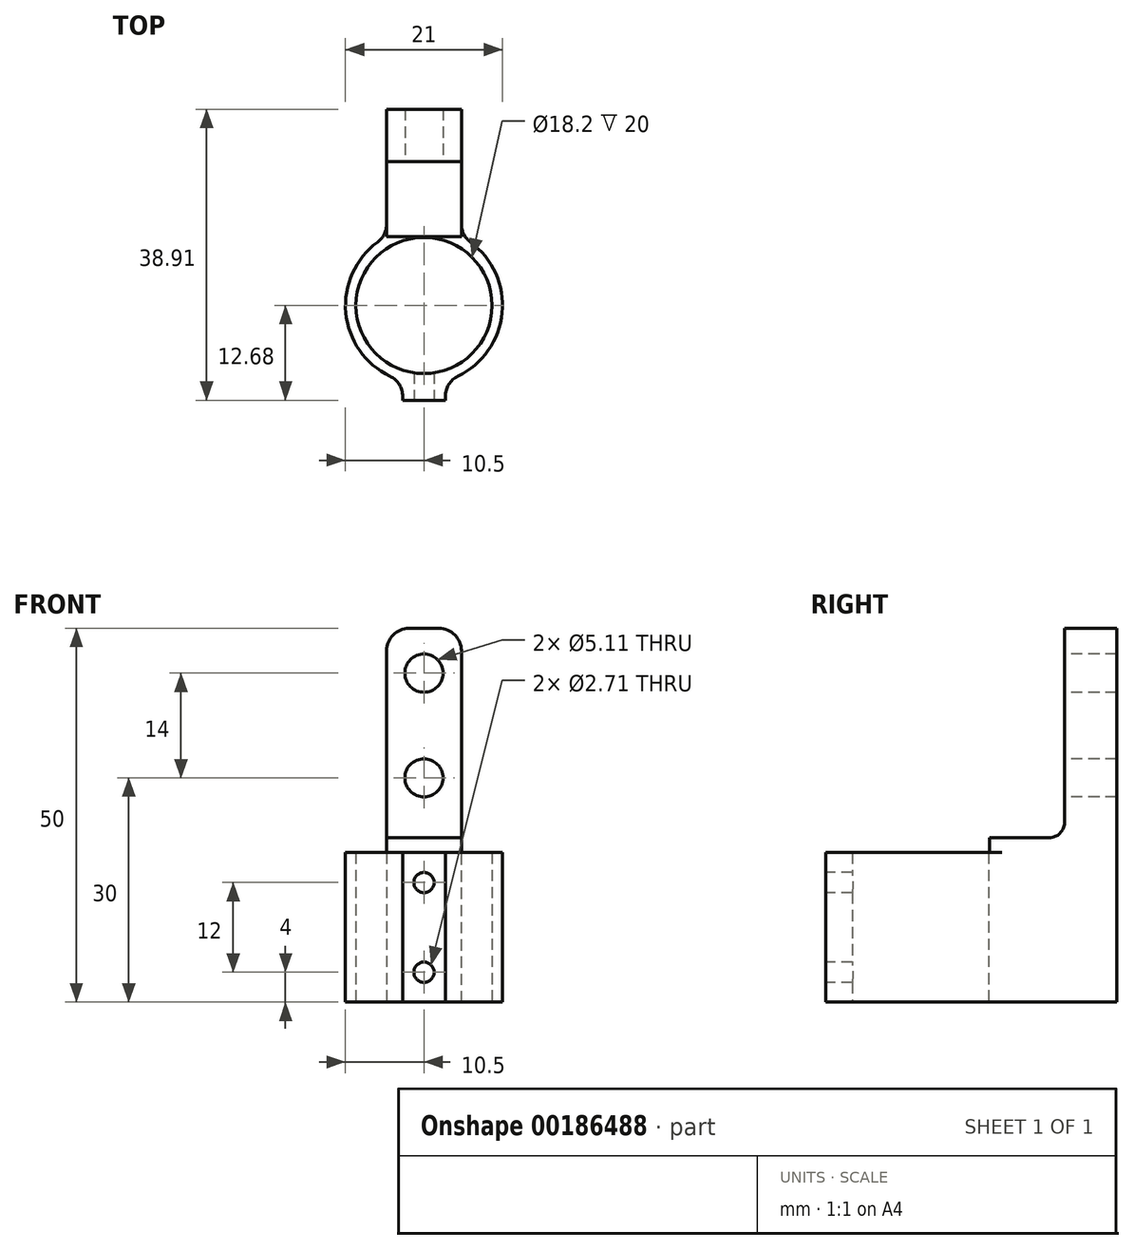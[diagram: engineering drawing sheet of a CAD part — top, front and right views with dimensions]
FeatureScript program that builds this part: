
annotation { "Feature Type Name" : "Feature", "Feature Type Description" : "" }
export const myFeature = defineFeature(function(context is Context, id is Id, definition is map)
    precondition{}
    {
        {
            var Q0;
            Q0=qCreatedBy(makeId("Top.planeOp"),FACE);
            var sketch = newSketch(context, id + "F0", { "sketchPlane" : qUnion([Q0])});
            skCircle(sketch, "E0", {"center": v(0, 0) * mm, "radius": 9.1 * mm});
            skCircle(sketch, "E1", {"center": v(0, 0) * mm, "radius": 10.5 * mm});
            skLineSegment(sketch, "E2.bottom", {"start": v(5, 9.23) * mm, "end": v(-5, 9.23) * mm});
            skLineSegment(sketch, "E2.top", {"start": v(5, 26.23) * mm, "end": v(-5, 26.23) * mm});
            skLineSegment(sketch, "E2.left", {"start": v(5, 9.23) * mm, "end": v(5, 26.23) * mm});
            skLineSegment(sketch, "E2.right", {"start": v(-5, 9.23) * mm, "end": v(-5, 26.23) * mm});
            skLineSegment(sketch, "E3.bottom", {"start": v(-2.85, -10.1) * mm, "end": v(2.85, -10.1) * mm});
            skLineSegment(sketch, "E3.top", {"start": v(-2.85, -12.68) * mm, "end": v(2.85, -12.68) * mm});
            skLineSegment(sketch, "E3.left", {"start": v(-2.85, -10.1) * mm, "end": v(-2.85, -12.68) * mm});
            skLineSegment(sketch, "E3.right", {"start": v(2.85, -10.1) * mm, "end": v(2.85, -12.68) * mm});
            skSolve(sketch);
        }
        {
            var Q0;
            Q0=qSketchRegion(id+"F0",true);
            extrude(context, id + "F1", {"entities" : qUnion([Q0]), "depth" : 20 * mm});
        }
        {
            var Q0;
            Q0=makeQuery(id+"F1.opExtrude","CAP_FACE",FACE,{"disambiguationData":[OSD([sQuery(id+"F0.wireOp",EDGE,"E0"),sQuery(id+"F0.wireOp",EDGE,"E1"),sQuery(id+"F0.wireOp",EDGE,"E2.top"),sQuery(id+"F0.wireOp",EDGE,"E2.left"),sQuery(id+"F0.wireOp",EDGE,"Skpy10Sz-M8vA-u5j2-6a00-2GGWUu09V0g2.top"),sQuery(id+"F0.wireOp",EDGE,"Skpy10Sz-M8vA-u5j2-6a00-2GGWUu09V0g2.left"),sQuery(id+"F0.wireOp",EDGE,"Skpy10Sz-M8vA-u5j2-6a00-2GGWUu09V0g2.right")])],"isStart":false});
            var sketch = newSketch(context, id + "F2", { "sketchPlane" : qUnion([Q0])});
            skLineSegment(sketch, "E4.bottom", {"start": v(5, 26.23) * mm, "end": v(-5, 26.23) * mm});
            skLineSegment(sketch, "E4.top", {"start": v(5, 9.23) * mm, "end": v(-5, 9.23) * mm});
            skLineSegment(sketch, "E4.left", {"start": v(5, 26.23) * mm, "end": v(5, 9.23) * mm});
            skLineSegment(sketch, "E4.right", {"start": v(-5, 26.23) * mm, "end": v(-5, 9.23) * mm});
            skSolve(sketch);
        }
        {
            var Q0;
            Q0=qSketchRegion(id+"F2",true);
            extrude(context, id + "F3", {"entities" : qUnion([Q0]), "operationType" : NewBodyOperationType.ADD, "depth" : 30 * mm});
        }
        {
            var Q0;
            Q0=makeQuery(id+"F3.boolean.opBoolean","MERGE",FACE,{"derivedFrom":[makeQuery(id+"F1.opExtrude","SWEPT_FACE",FACE,{"disambiguationData":[OSD([sQuery(id+"F0.wireOp",EDGE,"E2.left")])]}),makeQuery(id+"F3.opExtrude","SWEPT_FACE",FACE,{"disambiguationData":[OSD([sQuery(id+"F2.wireOp",EDGE,"E4.left")])]})]});
            var sketch = newSketch(context, id + "F4", { "sketchPlane" : qUnion([Q0])});
            skLineSegment(sketch, "E5.bottom", {"start": v(9.23, 50) * mm, "end": v(19.23, 50) * mm});
            skLineSegment(sketch, "E5.top", {"start": v(9.23, 22) * mm, "end": v(19.23, 22) * mm});
            skLineSegment(sketch, "E5.left", {"start": v(9.23, 50) * mm, "end": v(9.23, 22) * mm});
            skLineSegment(sketch, "E5.right", {"start": v(19.23, 50) * mm, "end": v(19.23, 22) * mm});
            skSolve(sketch);
        }
        {
            var Q0;
            Q0 = qSketchRegion(id + "F4", true);
            extrude(context, id + "F5", {"entities" : qUnion([Q0]), "operationType" : NewBodyOperationType.REMOVE, "oppositeDirection" : true, "depth" : 25.4 * mm});
        }
        {
            var Q0;
            Q0=makeQuery(id+"F1.opExtrude","SWEPT_EDGE",EDGE,{"disambiguationData":[OSD([sQuery(id+"F0.wireOp",EDGE,"E1"),sQuery(id+"F0.wireOp",EDGE,"E2.bottom"),sQuery(id+"F0.wireOp",EDGE,"E2.left")])]});
            var Q1;
            Q1=makeQuery(id+"F1.opExtrude","SWEPT_EDGE",EDGE,{"disambiguationData":[OSD([sQuery(id+"F0.wireOp",EDGE,"E1"),sQuery(id+"F0.wireOp",EDGE,"E2.bottom"),sQuery(id+"F0.wireOp",EDGE,"E2.right")])]});
            var Q2;
            Q2=makeQuery(id+"F3.opExtrude","CAP_EDGE",EDGE,{"disambiguationData":[OSD([sQuery(id+"F2.wireOp",EDGE,"E4.right")])],"isStart":false});
            var Q3;
            Q3=makeQuery(id+"F3.opExtrude","CAP_EDGE",EDGE,{"disambiguationData":[OSD([sQuery(id+"F2.wireOp",EDGE,"E4.left")])],"isStart":false});
            var Q4;
            Q4=makeQuery(id+"F1.opExtrude","SWEPT_EDGE",EDGE,{"disambiguationData":[OSD([sQuery(id+"F0.wireOp",EDGE,"E1"),sQuery(id+"F0.wireOp",EDGE,"E3.bottom"),sQuery(id+"F0.wireOp",EDGE,"E3.right")])]});
            var Q5;
            Q5=makeQuery(id+"F1.opExtrude","SWEPT_EDGE",EDGE,{"disambiguationData":[OSD([sQuery(id+"F0.wireOp",EDGE,"E1"),sQuery(id+"F0.wireOp",EDGE,"E3.bottom"),sQuery(id+"F0.wireOp",EDGE,"E3.left")])]});
            fillet(context, id + "F6", {"entities" : qUnion([Q0, Q1, Q2, Q3, Q4, Q5]), "radius" : 3 * mm, "tangentPropagation" : true, "allowEdgeOverflow" : false});
        }
        {
            var Q0;
            Q0=makeQuery(id+"F5.boolean.opBoolean","COPY",EDGE,{"derivedFrom":makeQuery(id+"F5.opExtrude","SWEPT_EDGE",EDGE,{"disambiguationData":[OSD([sQuery(id+"F0.wireOp",EDGE,"E1"),sQuery(id+"F2.wireOp",EDGE,"E4.top"),sQuery(id+"F2.wireOp",EDGE,"E4.left"),sQuery(id+"F4.wireOp",EDGE,"E5.top"),sQuery(id+"F4.wireOp",EDGE,"E5.left")])]})});
            var Q1;
            Q1=makeQuery(id+"F5.boolean.opBoolean","COPY",EDGE,{"derivedFrom":makeQuery(id+"F5.opExtrude","SWEPT_EDGE",EDGE,{"disambiguationData":[OSD([sQuery(id+"F4.wireOp",EDGE,"E5.top"),sQuery(id+"F4.wireOp",EDGE,"E5.right")])]})});
            fillet(context, id + "F7", {"entities" : qUnion([Q0, Q1]), "radius" : 2 * mm, "tangentPropagation" : true, "allowEdgeOverflow" : false});
        }
        {
            var Q0;
            Q0=makeQuery(id+"F5.boolean.opBoolean","COPY",FACE,{"derivedFrom":makeQuery(id+"F5.opExtrude","SWEPT_FACE",FACE,{"disambiguationData":[OSD([sQuery(id+"F4.wireOp",EDGE,"E5.right")])]})});
            var sketch = newSketch(context, id + "F8", { "sketchPlane" : qUnion([Q0])});
            skCircle(sketch, "E6", {"center": v(0, 44) * mm, "radius": 2.55 * mm});
            skCircle(sketch, "E7", {"center": v(0, 30) * mm, "radius": 2.55 * mm});
            skLineSegment(sketch, "E8", {"start": v(0, 50) * mm, "end": v(0, 37) * mm, "construction": true});
            skLineSegment(sketch, "E9", {"start": v(0, 37) * mm, "end": v(0, 24) * mm, "construction": true});
            skSolve(sketch);
        }
        {
            var Q0;
            Q0 = qSketchRegion(id + "F8", true);
            extrude(context, id + "F9", {"entities" : qUnion([Q0]), "operationType" : NewBodyOperationType.REMOVE, "endBound" : BoundingType.THROUGH_ALL, "oppositeDirection" : true, "depth" : 25.4 * mm});
        }
        {
            var Q0;
            Q0=makeQuery(id+"F1.opExtrude","SWEPT_FACE",FACE,{"disambiguationData":[OSD([sQuery(id+"F0.wireOp",EDGE,"E3.top")])]});
            var sketch = newSketch(context, id + "F10", { "sketchPlane" : qUnion([Q0])});
            skCircle(sketch, "E10", {"center": v(0, 16) * mm, "radius": 1.35 * mm});
            skCircle(sketch, "E11", {"center": v(0, 4) * mm, "radius": 1.35 * mm});
            skLineSegment(sketch, "E12", {"start": v(0, 20) * mm, "end": v(0, 10) * mm, "construction": true});
            skPoint(sketch, "E12.endSnap0", {"position": v(0, 20) * mm});
            skLineSegment(sketch, "E13", {"start": v(0, 10) * mm, "end": v(0, 0) * mm, "construction": true});
            skLineSegment(sketch, "E14", {"start": v(0, 0) * mm, "end": v(-0.09, -0.22) * mm, "construction": true});
            skSolve(sketch);
        }
        {
            var Q0;
            Q0 = qSketchRegion(id + "F10", true);
            extrude(context, id + "F11", {"entities" : qUnion([Q0]), "operationType" : NewBodyOperationType.REMOVE, "endBound" : BoundingType.UP_TO_NEXT, "oppositeDirection" : true, "depth" : 25.4 * mm});
        }
    });
